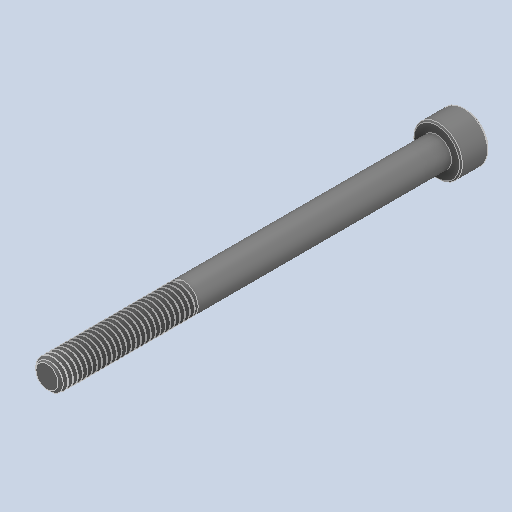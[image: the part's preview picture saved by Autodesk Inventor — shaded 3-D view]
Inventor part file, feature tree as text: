
AUTODESK INVENTOR PART (.ipt)
format: ipt  version: 2023.2 (Build 272271000, 271)  size: 666,624 bytes
history: native  units: in
note: dims shown in document units (in); Inventor stores cm internally (conversion verified against a paired STEP export)
features: chamfer x1
ambient origin geometry x8: Origin, YZ Plane, XZ Plane, XY Plane, X Axis, Y Axis, Z Axis, Center Point
bodies: Solid1 (feature_tree)
feature tree (1):
  chamfer  "Chamfer2"  [1 undecoded]
note: 1 required parameter value undecoded (feature->parameter linkage not recoverable at this tier; creation-order binding heuristic only, values carry confidence <= 0.55)
